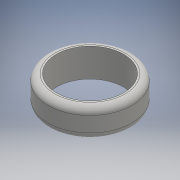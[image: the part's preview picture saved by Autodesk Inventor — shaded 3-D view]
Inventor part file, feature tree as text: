
AUTODESK INVENTOR PART (.ipt)
format: ipt  version: 2016 (Build 200138000, 138)  size: 129,024 bytes
history: native  units: mm
features: other x1, extrude x1, fillet x1, sketch x1
ambient origin geometry x8: Origin, YZ Plane, XZ Plane, XY Plane, X Axis, Y Axis, Z Axis, Center Point
bodies: Body1 (feature_tree)
feature tree (4):
  other  "ソリッド1"
  extrude  "押し出し1"  Depth=25.0mm
  fillet  "フィレット1"  Radius=20.0mm
  sketch  "スケッチ1"
